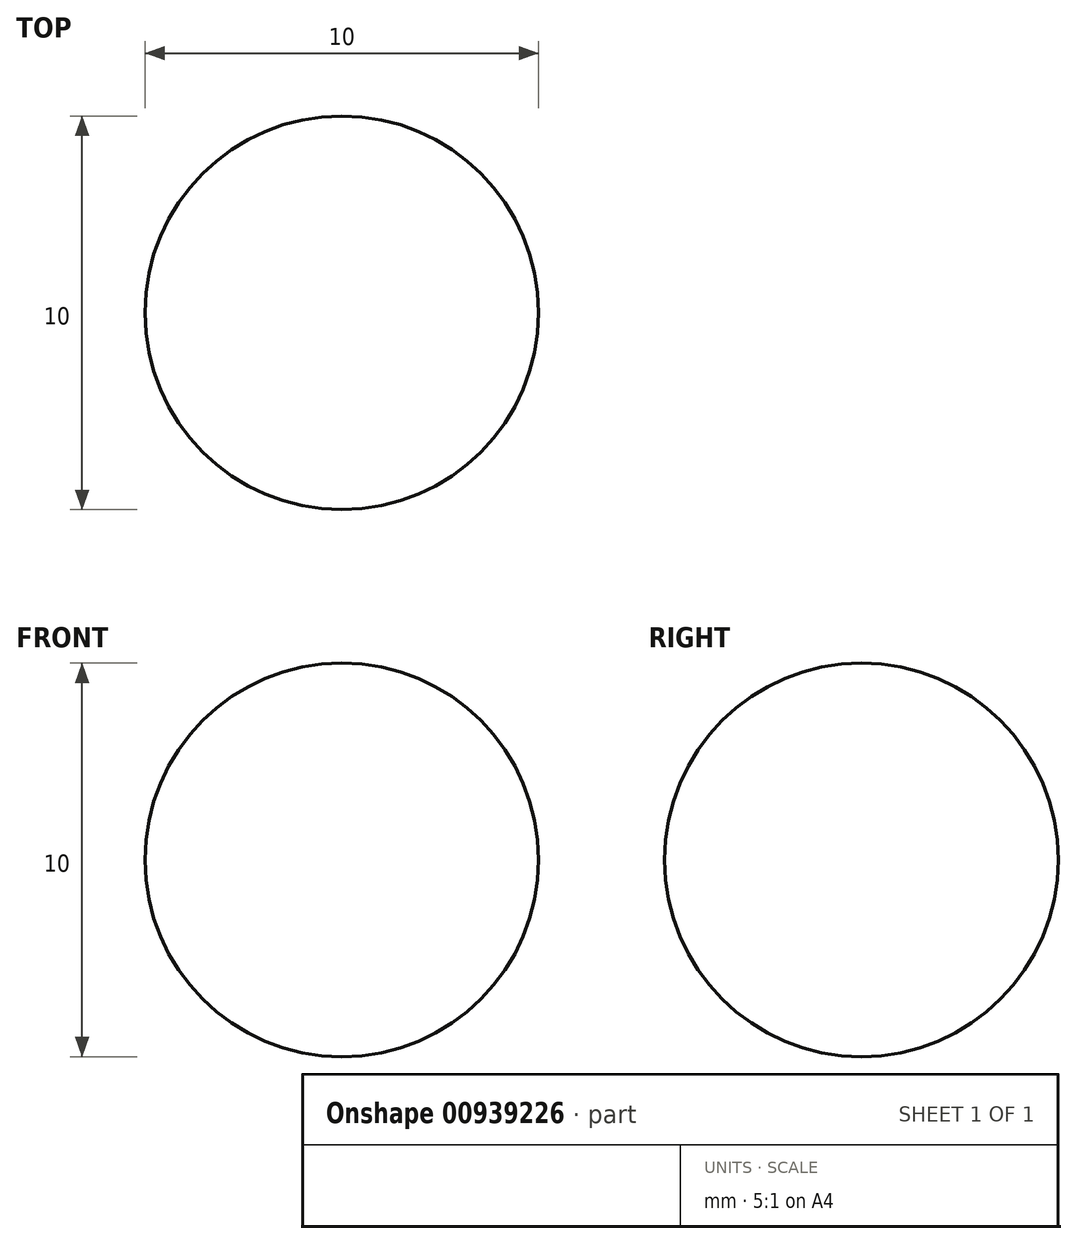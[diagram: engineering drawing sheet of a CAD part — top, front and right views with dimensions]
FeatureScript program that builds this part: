
annotation { "Feature Type Name" : "Feature", "Feature Type Description" : "" }
export const myFeature = defineFeature(function(context is Context, id is Id, definition is map)
    precondition{}
    {
        {
            var Q0;
            Q0=qCreatedBy(makeId("Top.planeOp"),FACE);
            var sketch = newSketch(context, id + "F0", { "sketchPlane" : qUnion([Q0])});
            skArc(sketch, "E0", {"start": v(0, -5) * mm, "mid": v(5, 0) * mm, "end": v(0, 5) * mm});
            skLineSegment(sketch, "E1", {"start": v(0, 5) * mm, "end": v(0, -5) * mm});
            skSolve(sketch);
        }
        {
            var Q0;
            Q0=makeQuery(id+"F0.imprint","IMPRINT",FACE,{"disambiguationData":[TD([[makeQuery(id+"F0.imprint","IMPRINT",EDGE,{"derivedFrom":sQuery(id+"F0.wireOp",EDGE,"E0")}),1.0]])]});
            var Q1;
            Q1=sQuery(id+"F0.wireOp",EDGE,"E1");
            revolve(context, id + "F1", {"surfaceOperationType" : NewSurfaceOperationType.NEW, "entities" : qUnion([Q0]), "axis" : qUnion([Q1]), "revolveType" : RevolveType.FULL});
        }
    });
